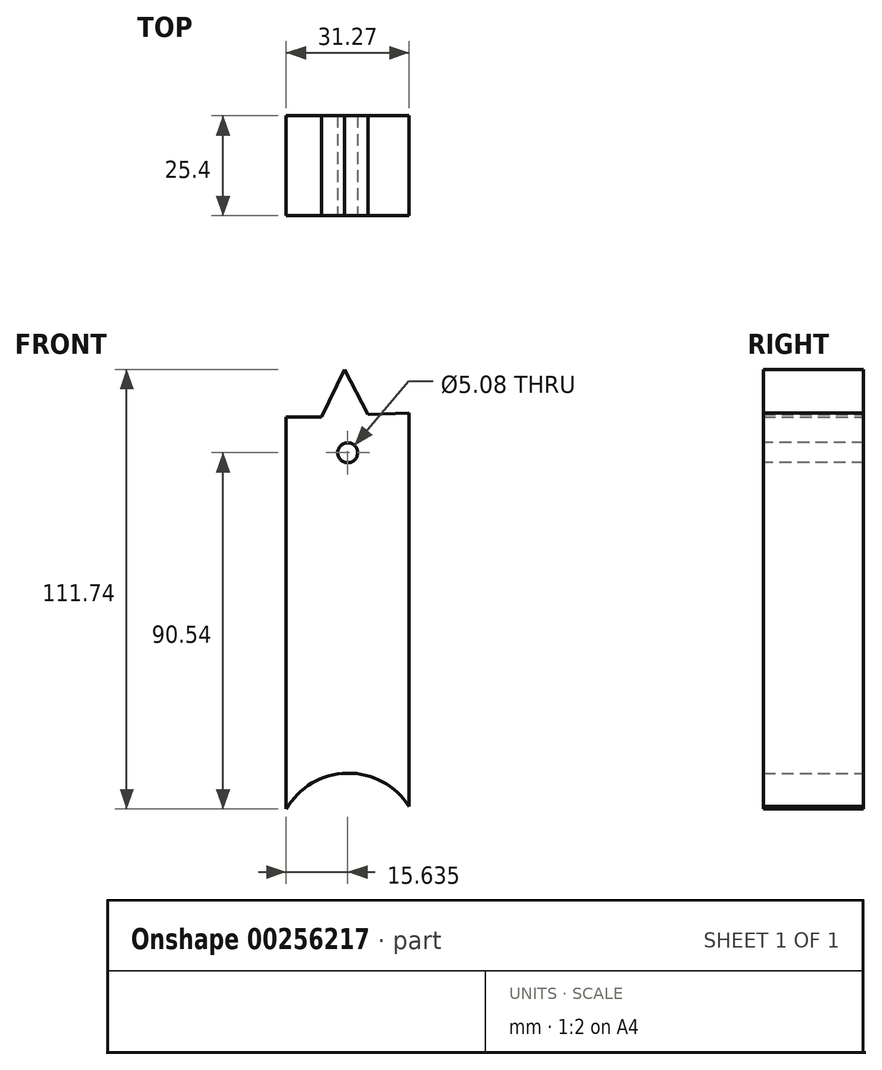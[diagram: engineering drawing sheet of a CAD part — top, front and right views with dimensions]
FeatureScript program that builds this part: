
annotation { "Feature Type Name" : "Feature", "Feature Type Description" : "" }
export const myFeature = defineFeature(function(context is Context, id is Id, definition is map)
    precondition{}
    {
        {
            var Q0;
            Q0=qCreatedBy(makeId("Front.planeOp"),FACE);
            var sketch = newSketch(context, id + "F0", { "sketchPlane" : qUnion([Q0])});
            skLineSegment(sketch, "E0", {"start": v(-8.98, 49.68) * mm, "end": v(-8.98, -49.99) * mm});
            skLineSegment(sketch, "E1", {"start": v(-8.98, 49.68) * mm, "end": v(0, 49.68) * mm});
            skLineSegment(sketch, "E2", {"start": v(11.76, 50.3) * mm, "end": v(5.88, 61.75) * mm});
            skLineSegment(sketch, "E3", {"start": v(0, 49.68) * mm, "end": v(5.88, 61.75) * mm});
            skPoint(sketch, "E4.start.orphan", {"position": v(18.26, -49.99) * mm});
            skLineSegment(sketch, "E5", {"start": v(22.29, -49.37) * mm, "end": v(22.29, 50.6) * mm});
            skLineSegment(sketch, "E6", {"start": v(11.76, 50.3) * mm, "end": v(22.29, 50.6) * mm});
            skArc(sketch, "E7", {"start": v(22.29, -49.37) * mm, "mid": v(6.48, -40.87) * mm, "end": v(-8.98, -49.99) * mm});
            skSolve(sketch);
        }
        {
            var Q0;
            Q0=makeQuery(id+"F0.imprint","IMPRINT",FACE,{"disambiguationData":[TD([[makeQuery(id+"F0.imprint","IMPRINT",EDGE,{"derivedFrom":sQuery(id+"F0.wireOp",EDGE,"E0")}),1.0]])]});
            extrude(context, id + "F1", {"entities" : qUnion([Q0]), "depth" : 25.4 * mm});
        }
        {
            var Q0;
            Q0=makeQuery(id+"F1.opExtrude","CAP_FACE",FACE,{"disambiguationData":[OSD([sQuery(id+"F0.wireOp",EDGE,"E0"),sQuery(id+"F0.wireOp",EDGE,"E1"),sQuery(id+"F0.wireOp",EDGE,"E2"),sQuery(id+"F0.wireOp",EDGE,"E3"),sQuery(id+"F0.wireOp",EDGE,"E5"),sQuery(id+"F0.wireOp",EDGE,"E6"),sQuery(id+"F0.wireOp",EDGE,"E7")])],"isStart":false});
            var sketch = newSketch(context, id + "F2", { "sketchPlane" : qUnion([Q0])});
            skLineSegment(sketch, "E8", {"start": v(-8.98, 40.55) * mm, "end": v(22.29, 40.55) * mm});
            skLineSegment(sketch, "E9", {"start": v(6.65, 40.55) * mm, "end": v(5.88, 61.75) * mm});
            skSolve(sketch);
        }
        {
            var Q0;
            Q0=sQuery(id+"F2.wireOp",VERTEX,"E9.start");
            var Q1;
            Q1=makeQuery(id+"F1.opExtrude","SWEPT_BODY",BODY,{"disambiguationData":[OSD([sQuery(id+"F0.wireOp",EDGE,"E0"),sQuery(id+"F0.wireOp",EDGE,"E1"),sQuery(id+"F0.wireOp",EDGE,"E2"),sQuery(id+"F0.wireOp",EDGE,"E3"),sQuery(id+"F0.wireOp",EDGE,"E5"),sQuery(id+"F0.wireOp",EDGE,"E6"),sQuery(id+"F0.wireOp",EDGE,"E7")])]});
            hole(context, id + "F3", {"style" : HoleStyle.SIMPLE, "endStyle" : HoleEndStyle.THROUGH, "holeDiameter" : 5.08 * mm, "tappedDepth" : 12.7 * mm, "tapClearance" : 3, "locations" : qUnion([Q0]), "scope" : qUnion([Q1])});
        }
    });
